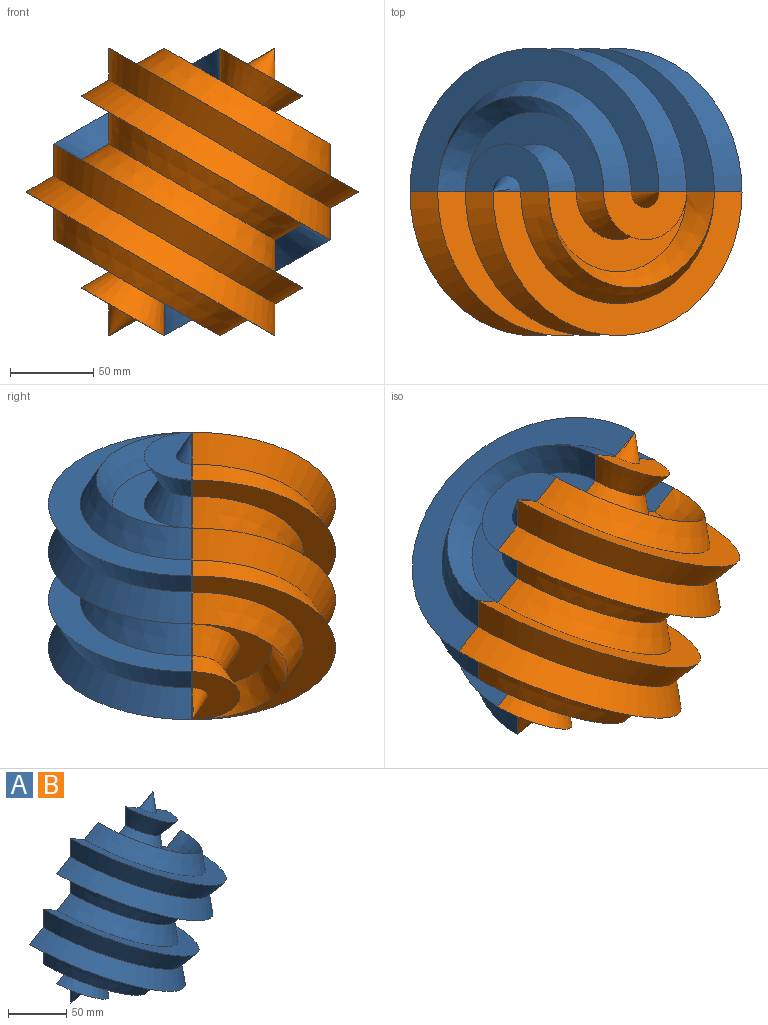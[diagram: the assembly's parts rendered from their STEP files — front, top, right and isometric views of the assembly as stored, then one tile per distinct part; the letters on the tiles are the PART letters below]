
ASSEMBLY  parts=2 mates=1
PART A: 25 faces, bbox 200x86.6x173.2 mm
  f0: cone r=0mm half-angle=30deg, axis (-0.5,0,-0.87), area 290.9mm2, adj f1,f24
  f1: plane 50x28.87mm, normal (0.5,0,0.87), area 1163.6mm2, adj f0,f2,f24
  f2: cone r=28.87mm half-angle=30deg, axis (0.5,0,0.87), area 1454.4mm2, adj f1,f3,f24
  f3: cone r=19.25mm half-angle=30deg, axis (-0.5,0,-0.87), area 1454.4mm2, adj f2,f4,f24
  f4: plane 83.33x48.11mm, normal (0.5,0,0.87), area 2327.1mm2, adj f3,f5,f24
  f5: cone r=48.11mm half-angle=30deg, axis (0.5,0,0.87), area 3199.8mm2, adj f4,f6,f24
  f6: cone r=57.74mm half-angle=30deg, axis (-0.5,0,-0.87), area 3781.5mm2, adj f5,f7,f24
  f7: plane 150x86.6mm, normal (0.5,0,0.87), area 4654.2mm2, adj f6,f8,f24
  f8: cone r=86.6mm half-angle=30deg, axis (0.5,0,0.87), area 4945.1mm2, adj f7,f9,f24
  f9: cone r=76.98mm half-angle=30deg, axis (-0.5,0,-0.87), area 4945.1mm2, adj f8,f10,f24
  f10: plane 150x86.6mm, normal (-0.5,0,-0.87), area 4654.2mm2, adj f9,f11,f24
  f11: cone r=67.36mm half-angle=30deg, axis (0.5,0,0.87), area 3781.5mm2, adj f10,f12,f24
  f12: cone r=57.74mm half-angle=30deg, axis (-0.5,0,-0.87), area 3781.5mm2, adj f11,f13,f24
  f13: plane 150x86.6mm, normal (0.5,0,0.87), area 4654.2mm2, adj f12,f14,f24
  f14: cone r=86.6mm half-angle=30deg, axis (0.5,0,0.87), area 4945.1mm2, adj f13,f15,f24
  f15: cone r=76.98mm half-angle=30deg, axis (-0.5,0,-0.87), area 4945.1mm2, adj f14,f16,f24
  f16: plane 150x86.6mm, normal (-0.5,0,-0.87), area 4654.2mm2, adj f15,f17,f24
  f17: cone r=67.36mm half-angle=30deg, axis (0.5,0,0.87), area 3781.5mm2, adj f16,f18,f24
  f18: cone r=57.74mm half-angle=30deg, axis (-0.5,0,-0.87), area 3199.8mm2, adj f17,f19,f24
  f19: plane 83.33x48.11mm, normal (-0.5,0,-0.87), area 2327.1mm2, adj f18,f20,f24
  f20: cone r=28.87mm half-angle=30deg, axis (0.5,0,0.87), area 1454.4mm2, adj f19,f21,f24
  f21: cone r=19.25mm half-angle=30deg, axis (-0.5,0,-0.87), area 1454.4mm2, adj f20,f22,f24
  f22: plane 50x28.87mm, normal (-0.5,0,-0.87), area 1163.6mm2, adj f21,f23,f24
  f23: cone r=9.62mm half-angle=30deg, axis (0.5,0,0.87), area 290.9mm2, adj f22,f24
  f24: plane 200x173.21mm, normal (0,1,0), area 19245mm2, adj f0,f1,f2,f3,f4,f5,f6,f7
PART B: same geometry as A
PLACE A rot(axis=(1,0,0),180deg) t=(0,0,0)mm
PLACE B at identity fixed
MATE fastened A.f24 <-> B.f24  axis (0,-1,0) through (0,0,0)mm
